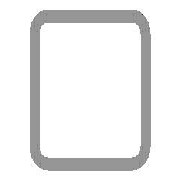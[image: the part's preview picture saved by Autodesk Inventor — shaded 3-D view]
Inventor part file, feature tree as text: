
AUTODESK INVENTOR PART (.ipt)
format: ipt  version: 2025 (Build 290162010, 162A)  size: 133,120 bytes
history: native  units: mm (DEFAULTED — no unit token found)
features: other x4, sketch x1, plane x1
ambient origin geometry x8: Origin, YZ Plane, XZ Plane, XY Plane, X Axis, Y Axis, Z Axis, Center Point
bodies: Solid1 (feature_tree), Body (feature_tree)
feature tree (6):
  parser-record x1  (decoder bookkeeping rows leaked as tree rows — omitted from the tree; the rows remain in map.json)
  other  "Driven Length"
  other  "Start Plane"
  other  "End Plane"
  sketch  "Sketch3"  dims[d3=858.0mm d4=0.0mm d7=4.0mm d9=40.0mm d11=40.0mm d12=2.0mm d13=40.0mm d14=898.0mm d15=20.0mm d16=20.0mm d17=90.0deg d18=858.0mm]
  plane  "Work Plane3"
